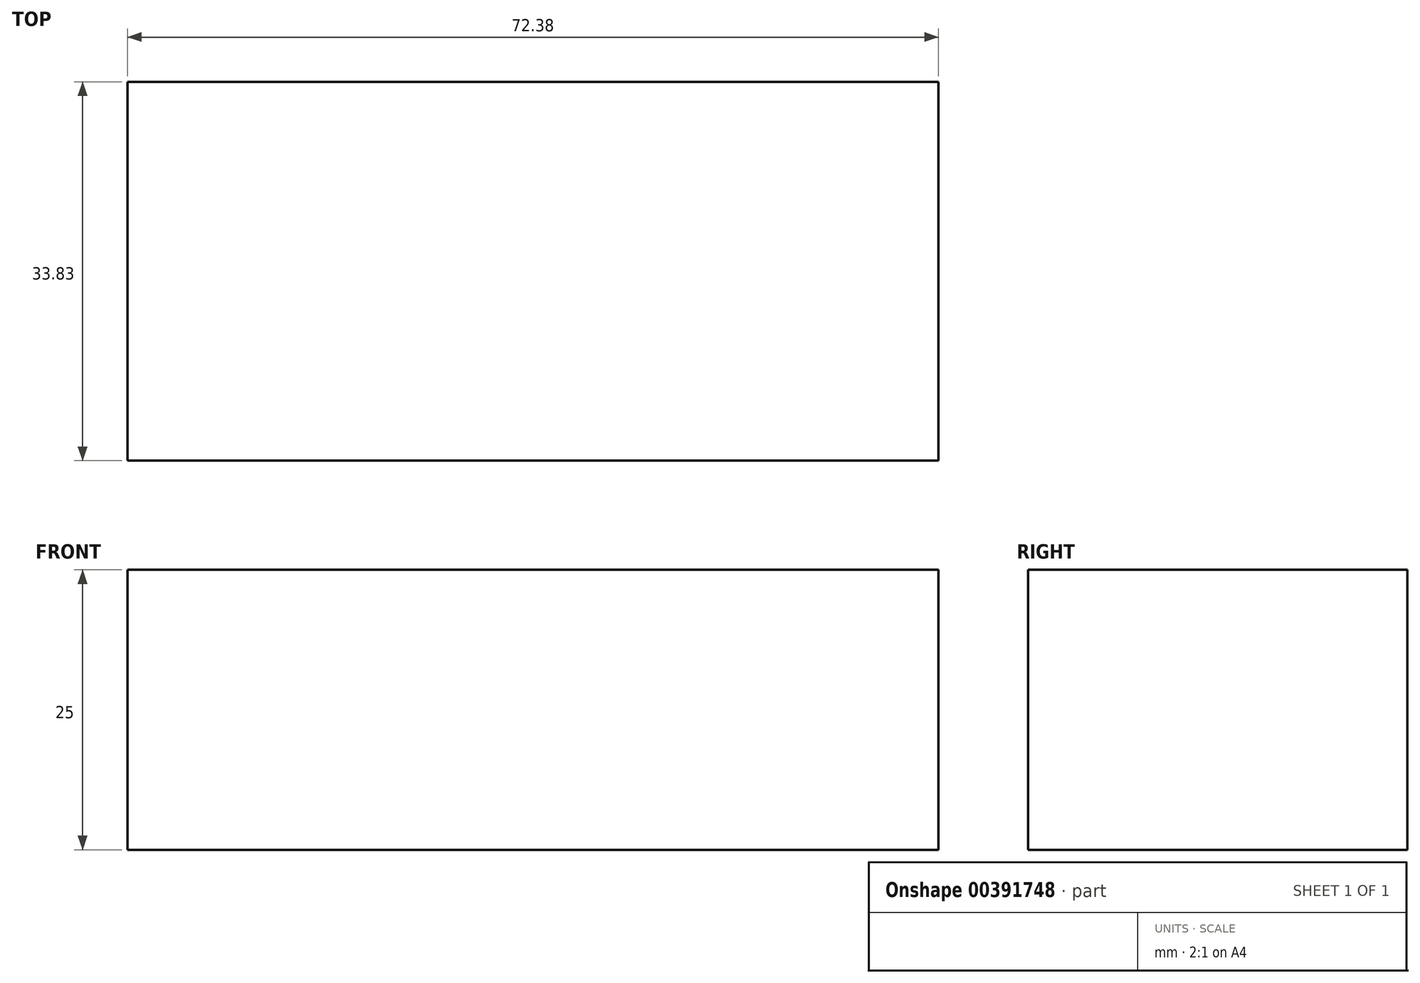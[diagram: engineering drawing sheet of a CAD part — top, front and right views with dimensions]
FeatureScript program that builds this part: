
annotation { "Feature Type Name" : "Feature", "Feature Type Description" : "" }
export const myFeature = defineFeature(function(context is Context, id is Id, definition is map)
    precondition{}
    {
        {
            var Q0;
            Q0=qCreatedBy(makeId("Top.planeOp"),FACE);
            var sketch = newSketch(context, id + "F0", { "sketchPlane" : qUnion([Q0])});
            skLineSegment(sketch, "E0.bottom", {"start": v(27.64, 13.1) * mm, "end": v(-44.74, 13.1) * mm});
            skLineSegment(sketch, "E0.top", {"start": v(27.64, 46.92) * mm, "end": v(-44.74, 46.92) * mm});
            skLineSegment(sketch, "E0.left", {"start": v(27.64, 13.1) * mm, "end": v(27.64, 46.92) * mm});
            skLineSegment(sketch, "E0.right", {"start": v(-44.74, 13.1) * mm, "end": v(-44.74, 46.92) * mm});
            skSolve(sketch);
        }
        {
            var Q0;
            Q0 = qSketchRegion(id + "F0", true);
            extrude(context, id + "F1", {"entities" : qUnion([Q0]), "depth" : 25 * mm});
        }
    });
